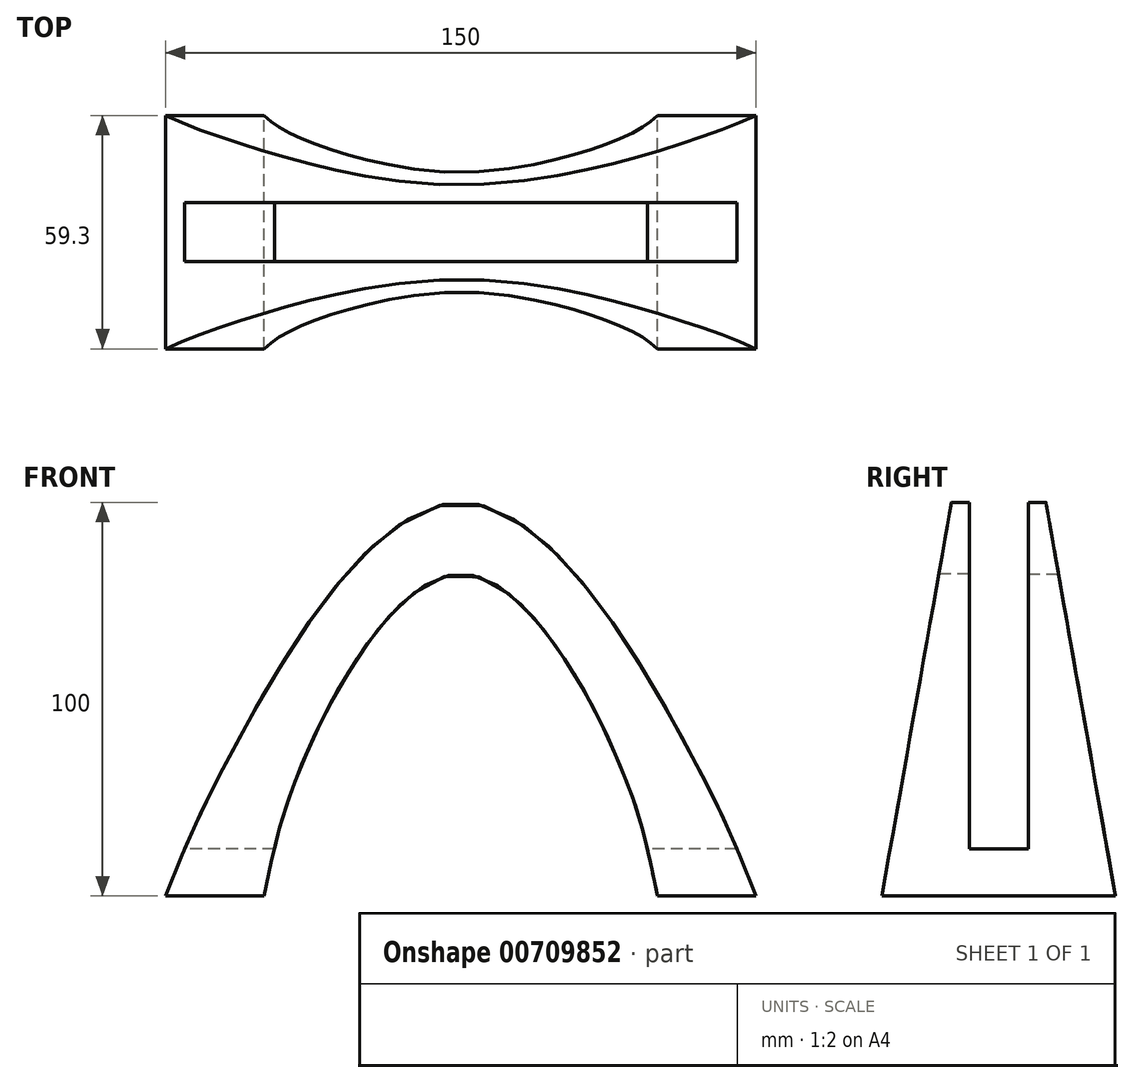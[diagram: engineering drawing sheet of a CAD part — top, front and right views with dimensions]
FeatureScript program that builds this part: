
annotation { "Feature Type Name" : "Feature", "Feature Type Description" : "" }
export const myFeature = defineFeature(function(context is Context, id is Id, definition is map)
    precondition{}
    {
        {
            var Q0;
            Q0=qCreatedBy(makeId("Right.planeOp"),FACE);
            var sketch = newSketch(context, id + "F0", { "sketchPlane" : qUnion([Q0])});
            skLineSegment(sketch, "E0", {"start": v(0, 0) * mm, "end": v(0, 168.18) * mm, "construction": true});
            skLineSegment(sketch, "E1", {"start": v(0, 0) * mm, "end": v(0, -68.18) * mm, "construction": true});
            skLineSegment(sketch, "E2", {"start": v(-29.65, 0) * mm, "end": v(29.65, 0) * mm});
            skLineSegment(sketch, "E3", {"start": v(-29.65, 0) * mm, "end": v(-12.02, 100) * mm});
            skLineSegment(sketch, "E4", {"start": v(29.65, 0) * mm, "end": v(12.02, 100) * mm});
            skLineSegment(sketch, "E5", {"start": v(-12.02, 100) * mm, "end": v(12.02, 100) * mm});
            skLineSegment(sketch, "E6", {"start": v(-41.68, -68.18) * mm, "end": v(-29.65, 0) * mm, "construction": true});
            skLineSegment(sketch, "E7", {"start": v(-12.02, 100) * mm, "end": v(0, 168.18) * mm, "construction": true});
            skLineSegment(sketch, "E8", {"start": v(-7.5, 100) * mm, "end": v(-7.5, 12) * mm});
            skLineSegment(sketch, "E9", {"start": v(-7.5, 12) * mm, "end": v(7.5, 12) * mm});
            skLineSegment(sketch, "E10", {"start": v(7.5, 12) * mm, "end": v(7.5, 100) * mm});
            skSolve(sketch);
        }
        {
            var Q0;
            Q0=qCreatedBy(makeId("Front.planeOp"),FACE);
            var sketch = newSketch(context, id + "F1", { "sketchPlane" : qUnion([Q0])});
            skFitSpline(sketch, "E11", {"points": [v(-75, 0) * mm, v(-58.37, 36.2) * mm, v(0, 100) * mm, v(58.37, 36.2) * mm, v(75, 0) * mm], "startDerivative": vector(99.4, 249.99) * mm, "endDerivative": vector(99.4, -249.99) * mm});
            skFitSpline(sketch, "E12", {"points": [v(-50, 0) * mm, v(-40.05, 34.27) * mm, v(0, 81.83) * mm, v(40.05, 34.27) * mm, v(50, 0) * mm], "startDerivative": vector(36.51, 166.77) * mm, "endDerivative": vector(36.51, -166.77) * mm});
            skLineSegment(sketch, "E13", {"start": v(-50, 0) * mm, "end": v(-75, 0) * mm});
            skLineSegment(sketch, "E14", {"start": v(50, 0) * mm, "end": v(75, 0) * mm});
            skLineSegment(sketch, "E15", {"start": v(0, 0) * mm, "end": v(0, 100) * mm, "construction": true});
            skSolve(sketch);
        }
        {
            var Q0;
            Q0=makeQuery(id+"F1.imprint","IMPRINT",FACE,{"disambiguationData":[TD([[makeQuery(id+"F1.imprint","IMPRINT",EDGE,{"derivedFrom":sQuery(id+"F1.wireOp",EDGE,"E11")}),-1.0]])]});
            var Q1;
            Q1=sQuery(id+"F0.wireOp",VERTEX,"E3.start");
            var Q2;
            Q2=sQuery(id+"F0.wireOp",VERTEX,"E4.start");
            extrude(context, id + "F2", {"entities" : qUnion([Q0]), "endBound" : BoundingType.UP_TO_VERTEX, "depth" : 50 * mm, "endBoundEntityVertex" : qUnion([Q1]), "offsetDistance" : 25 * mm, "hasSecondDirection" : true, "secondDirectionBound" : SecondDirectionBoundingType.UP_TO_VERTEX, "secondDirectionOppositeDirection" : true, "secondDirectionDepth" : 25 * mm, "secondDirectionBoundEntityVertex" : qUnion([Q2])});
        }
        {
            var Q0;
            Q0=makeQuery(id+"F0.imprint","IMPRINT",FACE,{"disambiguationData":[TD([[makeQuery(id+"F0.imprint","IMPRINT",EDGE,{"derivedFrom":sQuery(id+"F0.wireOp",EDGE,"E2")}),1.0]])]});
            extrude(context, id + "F3", {"entities" : qUnion([Q0]), "operationType" : NewBodyOperationType.INTERSECT, "endBound" : BoundingType.THROUGH_ALL, "depth" : 25 * mm, "offsetDistance" : 25 * mm, "hasSecondDirection" : true, "secondDirectionBound" : SecondDirectionBoundingType.THROUGH_ALL, "secondDirectionOppositeDirection" : true, "secondDirectionDepth" : 25 * mm});
        }
    });
